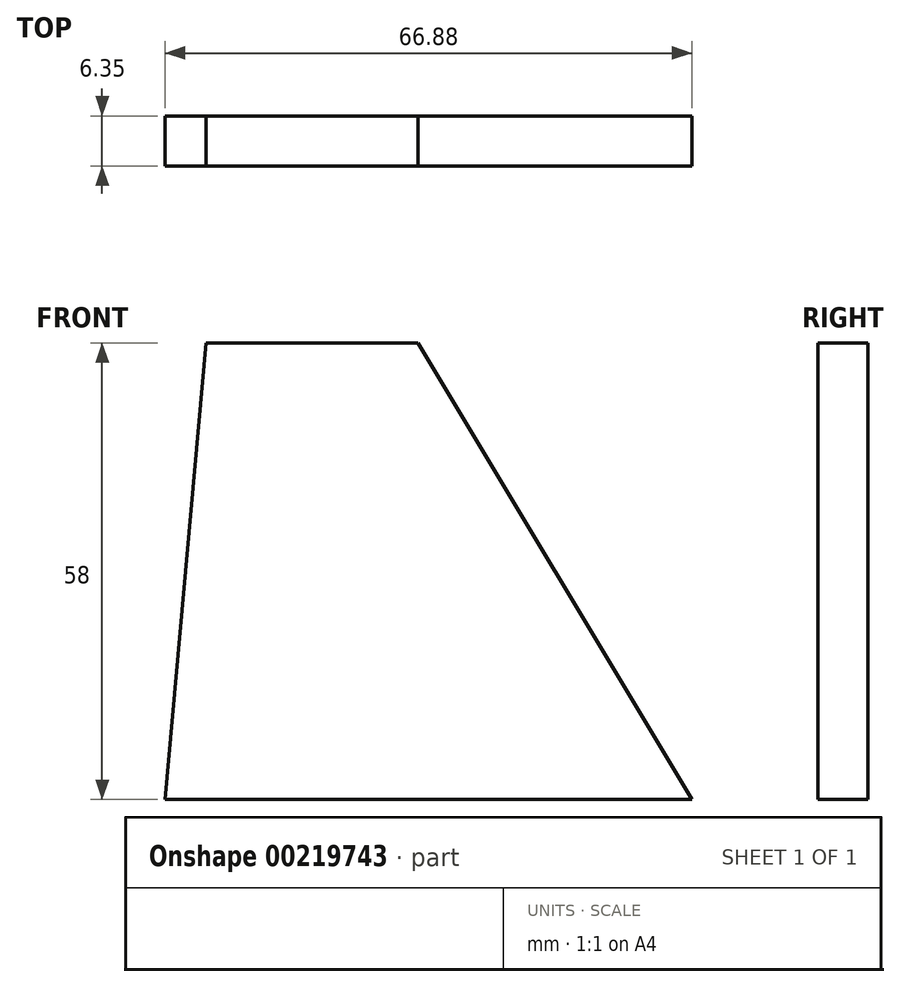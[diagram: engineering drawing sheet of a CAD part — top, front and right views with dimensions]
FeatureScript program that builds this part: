
annotation { "Feature Type Name" : "Feature", "Feature Type Description" : "" }
export const myFeature = defineFeature(function(context is Context, id is Id, definition is map)
    precondition{}
    {
        {
            var Q0;
            Q0=qCreatedBy(makeId("Front.planeOp"),FACE);
            var sketch = newSketch(context, id + "F0", { "sketchPlane" : qUnion([Q0])});
            skLineSegment(sketch, "E0", {"start": v(0, 0) * mm, "end": v(-66.88, 0) * mm});
            skLineSegment(sketch, "E1", {"start": v(-66.88, 0) * mm, "end": v(-61.7, 58) * mm});
            skLineSegment(sketch, "E2", {"start": v(-61.7, 58) * mm, "end": v(-34.75, 58) * mm});
            skLineSegment(sketch, "E3", {"start": v(-34.75, 58) * mm, "end": v(0, 0) * mm});
            skSolve(sketch);
        }
        {
            var Q0;
            Q0 = qSketchRegion(id + "F0", true);
            extrude(context, id + "F1", {"entities" : qUnion([Q0]), "depth" : 6.35 * mm});
        }
    });
